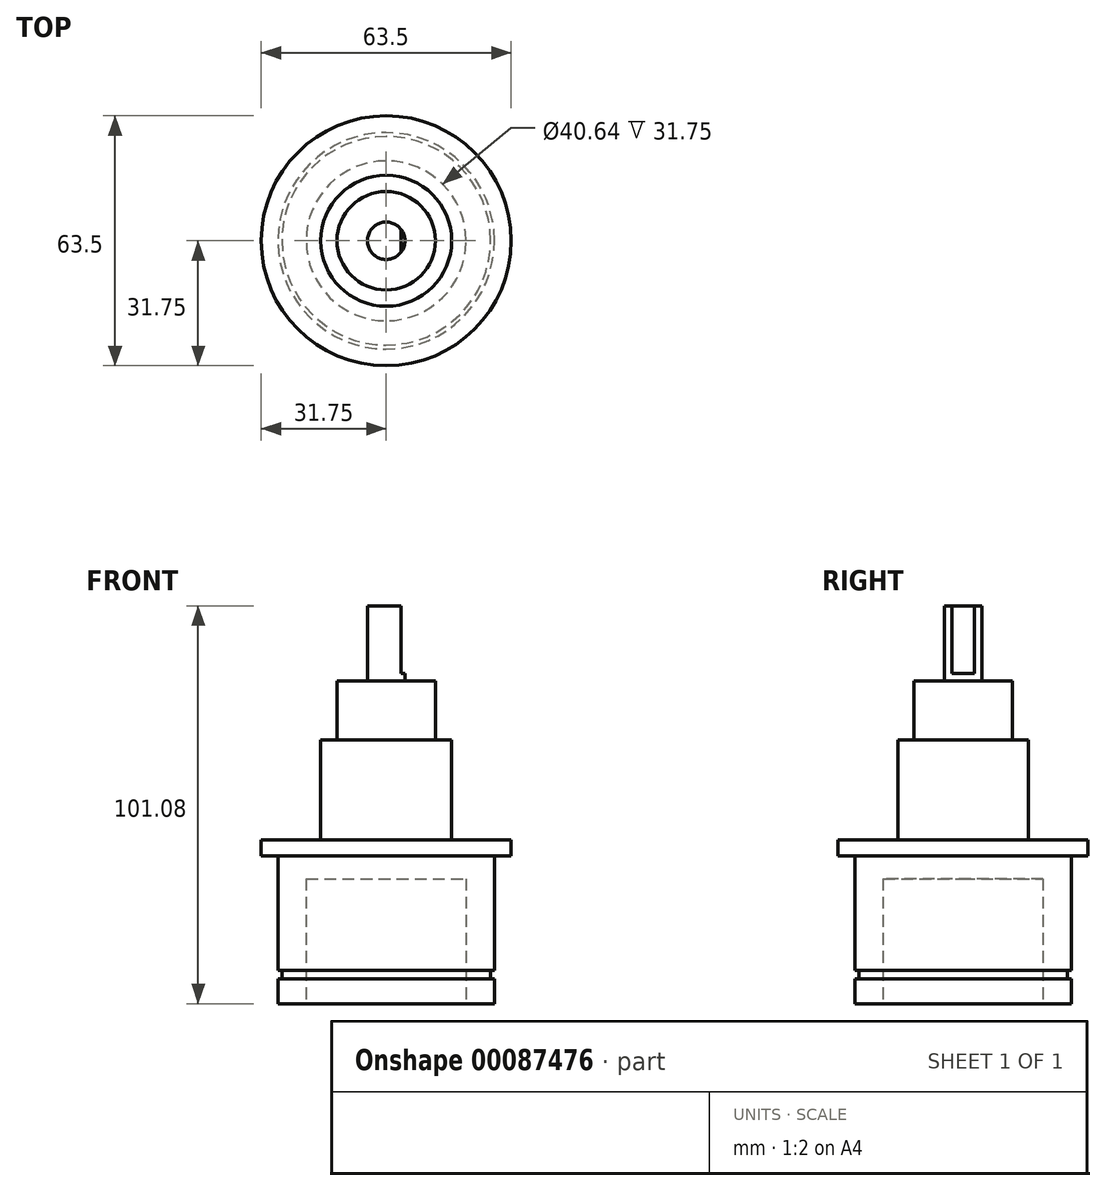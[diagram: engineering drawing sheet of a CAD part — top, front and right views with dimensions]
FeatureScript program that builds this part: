
annotation { "Feature Type Name" : "Feature", "Feature Type Description" : "" }
export const myFeature = defineFeature(function(context is Context, id is Id, definition is map)
    precondition{}
    {
        {
            var Q0;
            Q0=qCreatedBy(makeId("Front.planeOp"),FACE);
            var sketch = newSketch(context, id + "F0", { "sketchPlane" : qUnion([Q0])});
            skLineSegment(sketch, "E0", {"start": v(0, 0) * mm, "end": v(-4.76, 0) * mm});
            skLineSegment(sketch, "E1", {"start": v(-4.76, 0) * mm, "end": v(-4.76, -19.05) * mm});
            skLineSegment(sketch, "E2", {"start": v(-4.76, -19.05) * mm, "end": v(-12.5, -19.05) * mm});
            skLineSegment(sketch, "E3", {"start": v(-12.5, -19.05) * mm, "end": v(-12.5, -34.05) * mm});
            skLineSegment(sketch, "E4", {"start": v(-12.5, -34.05) * mm, "end": v(-16.63, -34.05) * mm});
            skLineSegment(sketch, "E5", {"start": v(-16.63, -34.05) * mm, "end": v(-16.63, -59.45) * mm});
            skLineSegment(sketch, "E6", {"start": v(-16.63, -59.45) * mm, "end": v(-31.75, -59.45) * mm});
            skLineSegment(sketch, "E7", {"start": v(-31.75, -59.45) * mm, "end": v(-31.75, -63.58) * mm});
            skLineSegment(sketch, "E8", {"start": v(-31.75, -63.58) * mm, "end": v(-27.5, -63.58) * mm});
            skLineSegment(sketch, "E9", {"start": v(-27.5, -63.58) * mm, "end": v(-27.5, -92.58) * mm});
            skLineSegment(sketch, "E10", {"start": v(-27.5, -101.08) * mm, "end": v(-20.32, -101.08) * mm});
            skLineSegment(sketch, "E11", {"start": v(0, -69.33) * mm, "end": v(0, 0) * mm});
            skLineSegment(sketch, "E12", {"start": v(-27.5, -92.58) * mm, "end": v(-26.5, -92.58) * mm});
            skLineSegment(sketch, "E13", {"start": v(-26.5, -92.58) * mm, "end": v(-26.5, -94.73) * mm});
            skLineSegment(sketch, "E14", {"start": v(-26.5, -94.73) * mm, "end": v(-27.5, -94.73) * mm});
            skLineSegment(sketch, "E15.trimOffspring", {"start": v(-27.5, -94.73) * mm, "end": v(-27.5, -101.08) * mm});
            skLineSegment(sketch, "E16", {"start": v(-20.32, -101.08) * mm, "end": v(-20.32, -69.33) * mm});
            skLineSegment(sketch, "E17", {"start": v(-20.32, -69.33) * mm, "end": v(0, -69.33) * mm});
            skPoint(sketch, "E18.orphan", {"position": v(0, -101.08) * mm});
            skSolve(sketch);
        }
        {
            var Q0;
            Q0 = qSketchRegion(id + "F0", true);
            var Q1;
            Q1=sQuery(id+"F0.wireOp",EDGE,"E11");
            revolve(context, id + "F1", {"entities" : qUnion([Q0]), "axis" : qUnion([Q1]), "revolveType" : RevolveType.FULL});
        }
        {
            var Q0;
            Q0=qCreatedBy(makeId("Right.planeOp"),FACE);
            cPlane(context, id + "F2", {"entities" : qUnion([Q0]), "cplaneType" : CPlaneType.OFFSET, "offset" : 3.8 * mm, "width" : 152.4 * mm, "height" : 152.4 * mm});
        }
        {
            var Q0;
            Q0=qCreatedBy(id+"F2.planeOp",FACE);
            var sketch = newSketch(context, id + "F3", { "sketchPlane" : qUnion([Q0])});
            skLineSegment(sketch, "E19", {"start": v(-4.76, -19.05) * mm, "end": v(-4.76, 0) * mm});
            skLineSegment(sketch, "E20", {"start": v(4.76, 0) * mm, "end": v(4.76, -19.05) * mm});
            skLineSegment(sketch, "E21", {"start": v(4.76, 0) * mm, "end": v(-4.76, 0) * mm});
            skLineSegment(sketch, "E22", {"start": v(-4.76, -17.15) * mm, "end": v(4.76, -17.15) * mm});
            skSolve(sketch);
        }
        {
            var Q0;
            Q0=makeQuery(id+"F3.imprint","IMPRINT",FACE,{"disambiguationData":[TD([[makeQuery(id+"F3.imprint","IMPRINT",EDGE,{"derivedFrom":sQuery(id+"F3.wireOp",EDGE,"E19")}),-1.0]])]});
            extrude(context, id + "F4", {"entities" : qUnion([Q0]), "operationType" : NewBodyOperationType.REMOVE, "endBound" : BoundingType.THROUGH_ALL, "depth" : 25.4 * mm});
        }
    });
